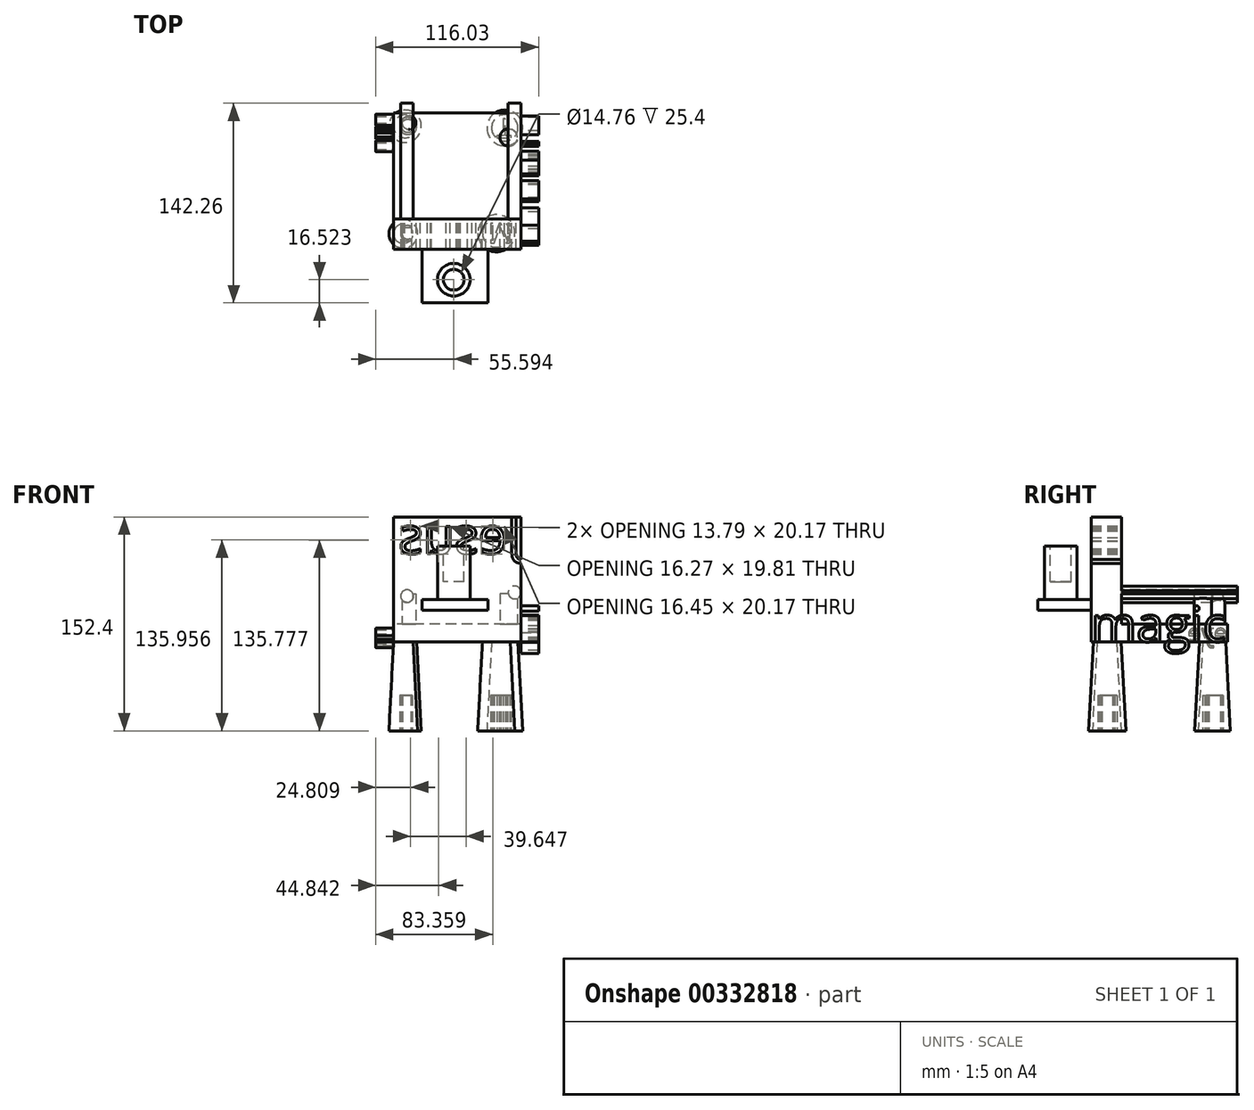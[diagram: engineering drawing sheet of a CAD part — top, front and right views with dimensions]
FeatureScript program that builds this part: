
annotation { "Feature Type Name" : "Feature", "Feature Type Description" : "" }
export const myFeature = defineFeature(function(context is Context, id is Id, definition is map)
    precondition{}
    {
        {
            var Q0;
            Q0=qCreatedBy(makeId("Top.planeOp"),FACE);
            var sketch = newSketch(context, id + "F0", { "sketchPlane" : qUnion([Q0])});
            skLineSegment(sketch, "E0.bottom", {"start": v(-47.1, -35.92) * mm, "end": v(43.53, -35.92) * mm});
            skLineSegment(sketch, "E0.top", {"start": v(-47.1, 61.4) * mm, "end": v(43.53, 61.4) * mm});
            skLineSegment(sketch, "E0.left", {"start": v(-47.1, -35.92) * mm, "end": v(-47.1, 61.4) * mm});
            skLineSegment(sketch, "E0.right", {"start": v(43.53, -35.92) * mm, "end": v(43.53, 61.4) * mm});
            skSolve(sketch);
        }
        {
            var Q0;
            Q0=makeQuery(id+"F0.imprint","IMPRINT",FACE,{"disambiguationData":[TD([[makeQuery(id+"F0.imprint","IMPRINT",EDGE,{"derivedFrom":sQuery(id+"F0.wireOp",EDGE,"E0.bottom")}),1.0]])]});
            extrude(context, id + "F1", {"entities" : qUnion([Q0]), "depth" : 12.7 * mm});
        }
        {
            var Q0;
            Q0=makeQuery(id+"F1.opExtrude","CAP_FACE",FACE,{"disambiguationData":[OSD([sQuery(id+"F0.wireOp",EDGE,"E0.bottom"),sQuery(id+"F0.wireOp",EDGE,"E0.top"),sQuery(id+"F0.wireOp",EDGE,"E0.left"),sQuery(id+"F0.wireOp",EDGE,"E0.right")])],"isStart":true});
            var sketch = newSketch(context, id + "F2", { "sketchPlane" : qUnion([Q0])});
            skCircle(sketch, "E1", {"center": v(-38.88, -51.86) * mm, "radius": 8.22 * mm});
            skSolve(sketch);
        }
        {
            var Q0;
            Q0 = qSketchRegion(id + "F2", true);
            extrude(context, id + "F3", {"entities" : qUnion([Q0]), "operationType" : NewBodyOperationType.ADD, "depth" : 63.5 * mm, "hasDraft" : true, "draftAngle" : 3 * degree});
        }
        {
            var Q0;
            Q0=makeQuery(id+"F1.opExtrude","CAP_FACE",FACE,{"disambiguationData":[OSD([sQuery(id+"F0.wireOp",EDGE,"E0.bottom"),sQuery(id+"F0.wireOp",EDGE,"E0.top"),sQuery(id+"F0.wireOp",EDGE,"E0.left"),sQuery(id+"F0.wireOp",EDGE,"E0.right")])],"isStart":true});
            var sketch = newSketch(context, id + "F4", { "sketchPlane" : qUnion([Q0])});
            skCircle(sketch, "E2", {"center": v(32.14, -50.66) * mm, "radius": 9.41 * mm});
            skSolve(sketch);
        }
        {
            var Q0;
            Q0 = qSketchRegion(id + "F4", true);
            extrude(context, id + "F5", {"entities" : qUnion([Q0]), "operationType" : NewBodyOperationType.ADD, "depth" : 63.5 * mm, "hasDraft" : true, "draftAngle" : 3 * degree});
        }
        {
            var Q0;
            Q0=makeQuery(id+"F1.opExtrude","CAP_FACE",FACE,{"disambiguationData":[OSD([sQuery(id+"F0.wireOp",EDGE,"E0.bottom"),sQuery(id+"F0.wireOp",EDGE,"E0.top"),sQuery(id+"F0.wireOp",EDGE,"E0.left"),sQuery(id+"F0.wireOp",EDGE,"E0.right")])],"isStart":true});
            var sketch = newSketch(context, id + "F6", { "sketchPlane" : qUnion([Q0])});
            skCircle(sketch, "E3", {"center": v(-40.2, 24.75) * mm, "radius": 6.9 * mm});
            skSolve(sketch);
        }
        {
            var Q0;
            Q0 = qSketchRegion(id + "F6", true);
            extrude(context, id + "F7", {"entities" : qUnion([Q0]), "operationType" : NewBodyOperationType.ADD, "depth" : 63.5 * mm, "hasDraft" : true, "draftAngle" : 3 * degree});
        }
        {
            var Q0;
            Q0=makeQuery(id+"F1.opExtrude","CAP_FACE",FACE,{"disambiguationData":[OSD([sQuery(id+"F0.wireOp",EDGE,"E0.bottom"),sQuery(id+"F0.wireOp",EDGE,"E0.top"),sQuery(id+"F0.wireOp",EDGE,"E0.left"),sQuery(id+"F0.wireOp",EDGE,"E0.right")])],"isStart":true});
            var sketch = newSketch(context, id + "F8", { "sketchPlane" : qUnion([Q0])});
            skCircle(sketch, "E4", {"center": v(26.11, 24.38) * mm, "radius": 9.9 * mm});
            skSolve(sketch);
        }
        {
            var Q0;
            Q0 = qSketchRegion(id + "F8", true);
            extrude(context, id + "F9", {"entities" : qUnion([Q0]), "operationType" : NewBodyOperationType.ADD, "depth" : 63.5 * mm, "hasDraft" : true, "draftAngle" : 3 * degree});
        }
        {
            var Q0;
            Q0=makeQuery(id+"F1.opExtrude","CAP_FACE",FACE,{"disambiguationData":[OSD([sQuery(id+"F0.wireOp",EDGE,"E0.bottom"),sQuery(id+"F0.wireOp",EDGE,"E0.top"),sQuery(id+"F0.wireOp",EDGE,"E0.left"),sQuery(id+"F0.wireOp",EDGE,"E0.right")])],"isStart":false});
            var sketch = newSketch(context, id + "F10", { "sketchPlane" : qUnion([Q0])});
            skLineSegment(sketch, "E5.bottom", {"start": v(43.53, -14.31) * mm, "end": v(-47.1, -14.31) * mm});
            skLineSegment(sketch, "E5.top", {"start": v(43.53, -35.92) * mm, "end": v(-47.1, -35.92) * mm});
            skLineSegment(sketch, "E5.left", {"start": v(43.53, -14.31) * mm, "end": v(43.53, -35.92) * mm});
            skLineSegment(sketch, "E5.right", {"start": v(-47.1, -14.31) * mm, "end": v(-47.1, -35.92) * mm});
            skSolve(sketch);
        }
        {
            var Q0;
            Q0 = qSketchRegion(id + "F10", true);
            extrude(context, id + "F11", {"entities" : qUnion([Q0]), "operationType" : NewBodyOperationType.ADD, "depth" : 76.2 * mm});
        }
        {
            var Q0;
            Q0=makeQuery(id+"F11.opExtrude","SWEPT_FACE",FACE,{"disambiguationData":[OSD([sQuery(id+"F10.wireOp",EDGE,"E5.bottom")])]});
            var sketch = newSketch(context, id + "F12", { "sketchPlane" : qUnion([Q0])});
            skCircle(sketch, "E6", {"center": v(-39.12, 35.17) * mm, "radius": 4.54 * mm});
            skSolve(sketch);
        }
        {
            var Q0;
            {var subQ0=sQuery(id+"F12.wireOp",EDGE,"E6");var subQ1=makeQuery(id+"F11.opExtrude","SWEPT_EDGE",EDGE,{"disambiguationData":[OSD([sQuery(id+"F0.wireOp",EDGE,"E0.right"),sQuery(id+"F10.wireOp",EDGE,"E5.bottom"),sQuery(id+"F10.wireOp",EDGE,"E5.left")])]});var subQ2=makeQuery(id+"F12.imprint","INTERSECT",VERTEX,{"disambiguationData":[OD(0.0)],"derivedFrom":[subQ1,subQ0]});Q0=makeQuery(id+"F12.imprint","IMPRINT",FACE,{"disambiguationData":[TD([[makeQuery(id+"F12.imprint","IMPRINT",EDGE,{"disambiguationData":[TD([[subQ2,1.0]])],"derivedFrom":subQ0}),1.0]])]});}
            extrude(context, id + "F13", {"entities" : qUnion([Q0]), "operationType" : NewBodyOperationType.ADD, "depth" : 82.55 * mm});
        }
        {
            var Q0;
            Q0=makeQuery(id+"F11.opExtrude","SWEPT_FACE",FACE,{"disambiguationData":[OSD([sQuery(id+"F10.wireOp",EDGE,"E5.bottom")])]});
            var sketch = newSketch(context, id + "F14", { "sketchPlane" : qUnion([Q0])});
            skCircle(sketch, "E7", {"center": v(37.5, 32.5) * mm, "radius": 4.5 * mm});
            skSolve(sketch);
        }
        {
            var Q0;
            Q0=makeQuery(id+"F14.imprint","IMPRINT",FACE,{"disambiguationData":[TD([[makeQuery(id+"F14.imprint","IMPRINT",EDGE,{"derivedFrom":sQuery(id+"F14.wireOp",EDGE,"E7")}),1.0]])]});
            extrude(context, id + "F15", {"entities" : qUnion([Q0]), "operationType" : NewBodyOperationType.ADD, "depth" : 82.55 * mm});
        }
        {
            var Q0;
            Q0=makeQuery(id+"F11.opExtrude","SWEPT_FACE",FACE,{"disambiguationData":[OSD([sQuery(id+"F10.wireOp",EDGE,"E5.bottom")])]});
            var sketch = newSketch(context, id + "F16", { "sketchPlane" : qUnion([Q0])});
            skText(sketch, "E8", { "text": "Jesus\n", "fontName": "OpenSans-Regular.ttf"});
            const initialGuessF16  = {"E8": [-0.04353, 0.06273, 1, 0, 0.02617]};
            skSetInitialGuess(sketch, initialGuessF16);
            skSolve(sketch);
        }
        {
            var Q0;
            Q0=makeQuery(id+"F16.imprint","IMPRINT",FACE,{"disambiguationData":[TD([[makeQuery(id+"F16.imprint","IMPRINT",EDGE,{"derivedFrom":sQuery(id+"F16.wireOp",EDGE,"E8.sketch_text.stroke-54")}),-1.0]])]});
            var Q1;
            Q1=makeQuery(id+"F16.imprint","IMPRINT",FACE,{"disambiguationData":[TD([[makeQuery(id+"F16.imprint","IMPRINT",EDGE,{"derivedFrom":sQuery(id+"F16.wireOp",EDGE,"E8.sketch_text.stroke-29")}),-1.0]])]});
            var Q2;
            {var subQ8=sQuery(id+"F16.wireOp",EDGE,"E8.sketch_text.stroke-4");Q2=makeQuery(id+"F16.imprint","IMPRINT",FACE,{"disambiguationData":[TD([[makeQuery(id+"F16.imprint","IMPRINT",EDGE,{"derivedFrom":subQ8}),-1.0]])]});}
            var Q3;
            Q3=makeQuery(id+"F16.imprint","IMPRINT",FACE,{"disambiguationData":[TD([[makeQuery(id+"F16.imprint","IMPRINT",EDGE,{"derivedFrom":sQuery(id+"F16.wireOp",EDGE,"E8.sketch_text.stroke-10")}),-1.0]])]});
            var Q4;
            Q4=makeQuery(id+"F16.imprint","IMPRINT",FACE,{"disambiguationData":[TD([[makeQuery(id+"F16.imprint","IMPRINT",EDGE,{"derivedFrom":sQuery(id+"F16.wireOp",EDGE,"E8.sketch_text.stroke-71")}),-1.0]])]});
            extrude(context, id + "F17", {"entities" : qUnion([Q0, Q1, Q2, Q3, Q4]), "operationType" : NewBodyOperationType.REMOVE, "oppositeDirection" : true, "depth" : 28.28 * mm});
        }
        {
            var Q0;
            {var subQ2=sQuery(id+"F10.wireOp",EDGE,"E5.bottom");var subQ4=sQuery(id+"F0.wireOp",EDGE,"E0.left");Q0=makeQuery(id+"F17.boolean.opBoolean","SPLIT",FACE,{"disambiguationData":[TD([makeQuery(id+"F1.opExtrude","SWEPT_FACE",FACE,{"disambiguationData":[OSD([subQ4])]})])],"derivedFrom":makeQuery(id+"F11.opExtrude","SWEPT_FACE",FACE,{"disambiguationData":[OSD([subQ2])]})});}
            var sketch = newSketch(context, id + "F18", { "sketchPlane" : qUnion([Q0])});
            skSolve(sketch);
        }
        {
            var Q0;
            Q0=makeQuery(id+"F5.opExtrude","CAP_FACE",FACE,{"disambiguationData":[OSD([sQuery(id+"F4.wireOp",EDGE,"E2")])],"isStart":false});
            var sketch = newSketch(context, id + "F19", { "sketchPlane" : qUnion([Q0])});
            skText(sketch, "E9", { "text": "T", "fontName": "OpenSans-Regular.ttf"});
            const initialGuessF19  = {"E9": [0.02645, -0.05722, 1, 0, 0.01368]};
            skSetInitialGuess(sketch, initialGuessF19);
            skSolve(sketch);
        }
        {
            var Q0;
            Q0 = qSketchRegion(id + "F19", true);
            extrude(context, id + "F20", {"entities" : qUnion([Q0]), "operationType" : NewBodyOperationType.REMOVE, "oppositeDirection" : true, "depth" : 25.4 * mm});
        }
        {
            var Q0;
            Q0=makeQuery(id+"F3.opExtrude","CAP_FACE",FACE,{"disambiguationData":[OSD([sQuery(id+"F2.wireOp",EDGE,"E1")])],"isStart":false});
            var sketch = newSketch(context, id + "F21", { "sketchPlane" : qUnion([Q0])});
            skText(sketch, "E10", { "text": "C", "fontName": "OpenSans-Regular.ttf"});
            const initialGuessF21  = {"E10": [-0.04366, -0.0579, 1, 0, 0.01173]};
            skSetInitialGuess(sketch, initialGuessF21);
            skSolve(sketch);
        }
        {
            var Q0;
            Q0 = qSketchRegion(id + "F21", true);
            extrude(context, id + "F22", {"entities" : qUnion([Q0]), "operationType" : NewBodyOperationType.REMOVE, "oppositeDirection" : true, "depth" : 25.4 * mm});
        }
        {
            var Q0;
            Q0=makeQuery(id+"F7.opExtrude","CAP_FACE",FACE,{"disambiguationData":[OSD([sQuery(id+"F6.wireOp",EDGE,"E3")])],"isStart":false});
            var sketch = newSketch(context, id + "F23", { "sketchPlane" : qUnion([Q0])});
            skText(sketch, "E11", { "text": "C", "fontName": "OpenSans-Regular.ttf"});
            const initialGuessF23  = {"E11": [-0.043, 0.01915, 1, 0, 0.01066]};
            skSetInitialGuess(sketch, initialGuessF23);
            skSolve(sketch);
        }
        {
            var Q0;
            Q0 = qSketchRegion(id + "F23", true);
            extrude(context, id + "F24", {"entities" : qUnion([Q0]), "operationType" : NewBodyOperationType.REMOVE, "oppositeDirection" : true, "depth" : 25.4 * mm});
        }
        {
            var Q0;
            Q0=makeQuery(id+"F9.opExtrude","CAP_FACE",FACE,{"disambiguationData":[OSD([sQuery(id+"F8.wireOp",EDGE,"E4")])],"isStart":false});
            var sketch = newSketch(context, id + "F25", { "sketchPlane" : qUnion([Q0])});
            skText(sketch, "E12", { "text": "M", "fontName": "OpenSans-Regular.ttf"});
            const initialGuessF25  = {"E12": [0.02017, 0.01745, 1, 0, 0.01387]};
            skSetInitialGuess(sketch, initialGuessF25);
            skSolve(sketch);
        }
        {
            var Q0;
            Q0 = qSketchRegion(id + "F25", true);
            extrude(context, id + "F26", {"entities" : qUnion([Q0]), "operationType" : NewBodyOperationType.REMOVE, "oppositeDirection" : true, "depth" : 25.4 * mm});
        }
        {
            var Q0;
            {var subQ0=sQuery(id+"F0.wireOp",EDGE,"E0.top");var subQ1=sQuery(id+"F10.wireOp",EDGE,"E5.bottom");var subQ2=sQuery(id+"F0.wireOp",EDGE,"E0.right");var subQ6=sQuery(id+"F10.wireOp",EDGE,"E5.left");Q0=makeQuery(id+"F17.boolean.opBoolean","SPLIT",FACE,{"disambiguationData":[TD([makeQuery(id+"F1.opExtrude","SWEPT_FACE",FACE,{"disambiguationData":[OSD([subQ0])]})])],"derivedFrom":makeQuery(id+"F13.boolean.opBoolean","MERGE",FACE,{"derivedFrom":[makeQuery(id+"F11.boolean.opBoolean","MERGE",FACE,{"derivedFrom":[makeQuery(id+"F1.opExtrude","SWEPT_FACE",FACE,{"disambiguationData":[OSD([subQ2])]}),makeQuery(id+"F11.opExtrude","SWEPT_FACE",FACE,{"disambiguationData":[OSD([subQ6])]})]}),makeQuery(id+"F13.opExtrude","SWEPT_FACE",FACE,{"disambiguationData":[OSD([subQ2,subQ1,subQ6])]})]})});}
            var sketch = newSketch(context, id + "F27", { "sketchPlane" : qUnion([Q0])});
            skText(sketch, "E13", { "text": "magic", "fontName": "OpenSans-Regular.ttf"});
            const initialGuessF27  = {"E13": [-0.03592, 0, 1, 0, 0.02508]};
            skSetInitialGuess(sketch, initialGuessF27);
            skSolve(sketch);
        }
        {
            var Q0;
            Q0 = qSketchRegion(id + "F27", true);
            extrude(context, id + "F28", {"entities" : qUnion([Q0]), "operationType" : NewBodyOperationType.ADD, "depth" : 12.7 * mm});
        }
        {
            var Q0;
            Q0=makeQuery(id+"F11.boolean.opBoolean","MERGE",FACE,{"derivedFrom":[makeQuery(id+"F1.opExtrude","SWEPT_FACE",FACE,{"disambiguationData":[OSD([sQuery(id+"F0.wireOp",EDGE,"E0.left")])]}),makeQuery(id+"F11.opExtrude","SWEPT_FACE",FACE,{"disambiguationData":[OSD([sQuery(id+"F10.wireOp",EDGE,"E5.right")])]})]});
            var sketch = newSketch(context, id + "F29", { "sketchPlane" : qUnion([Q0])});
            skText(sketch, "E14", { "text": "eye\n", "fontName": "OpenSans-Regular.ttf"});
            const initialGuessF29  = {"E14": [-0.0614, 0, 1, 0, 0.0127]};
            skSetInitialGuess(sketch, initialGuessF29);
            skSolve(sketch);
        }
        {
            var Q0;
            Q0 = qSketchRegion(id + "F29", true);
            extrude(context, id + "F30", {"entities" : qUnion([Q0]), "operationType" : NewBodyOperationType.ADD, "depth" : 12.7 * mm});
        }
        {
            var Q0;
            Q0=makeQuery(id+"F1.opExtrude","CAP_FACE",FACE,{"disambiguationData":[OSD([sQuery(id+"F0.wireOp",EDGE,"E0.bottom"),sQuery(id+"F0.wireOp",EDGE,"E0.top"),sQuery(id+"F0.wireOp",EDGE,"E0.left"),sQuery(id+"F0.wireOp",EDGE,"E0.right")])],"isStart":false});
            var sketch = newSketch(context, id + "F31", { "sketchPlane" : qUnion([Q0])});
            skCircle(sketch, "E15", {"center": v(-36.14, 54.44) * mm, "radius": 4.98 * mm});
            skSolve(sketch);
        }
        {
            var Q0;
            Q0 = qSketchRegion(id + "F31", true);
            extrude(context, id + "F32", {"entities" : qUnion([Q0]), "operationType" : NewBodyOperationType.ADD, "depth" : 21.59 * mm});
        }
        {
            var Q0;
            Q0=makeQuery(id+"F1.opExtrude","CAP_FACE",FACE,{"disambiguationData":[OSD([sQuery(id+"F0.wireOp",EDGE,"E0.bottom"),sQuery(id+"F0.wireOp",EDGE,"E0.top"),sQuery(id+"F0.wireOp",EDGE,"E0.left"),sQuery(id+"F0.wireOp",EDGE,"E0.right")])],"isStart":false});
            var sketch = newSketch(context, id + "F33", { "sketchPlane" : qUnion([Q0])});
            skCircle(sketch, "E16", {"center": v(34.91, 43.84) * mm, "radius": 6.2 * mm});
            skSolve(sketch);
        }
        {
            var Q0;
            Q0 = qSketchRegion(id + "F33", true);
            extrude(context, id + "F34", {"entities" : qUnion([Q0]), "operationType" : NewBodyOperationType.ADD, "depth" : 21.59 * mm});
        }
        {
            var Q0;
            {var subQ0=sQuery(id+"F0.wireOp",EDGE,"E0.left");var subQ5=sQuery(id+"F0.wireOp",EDGE,"E0.bottom");var subQ6=sQuery(id+"F10.wireOp",EDGE,"E5.top");Q0=makeQuery(id+"F17.boolean.opBoolean","SPLIT",FACE,{"disambiguationData":[TD([makeQuery(id+"F1.opExtrude","SWEPT_FACE",FACE,{"disambiguationData":[OSD([subQ0])]})])],"derivedFrom":makeQuery(id+"F11.boolean.opBoolean","MERGE",FACE,{"derivedFrom":[makeQuery(id+"F1.opExtrude","SWEPT_FACE",FACE,{"disambiguationData":[OSD([subQ5])]}),makeQuery(id+"F11.opExtrude","SWEPT_FACE",FACE,{"disambiguationData":[OSD([subQ6])]})]})});}
            var sketch = newSketch(context, id + "F35", { "sketchPlane" : qUnion([Q0])});
            skLineSegment(sketch, "E17.bottom", {"start": v(-26.87, 22.3) * mm, "end": v(20.1, 22.3) * mm});
            skLineSegment(sketch, "E17.top", {"start": v(-26.87, 29.97) * mm, "end": v(20.1, 29.97) * mm});
            skLineSegment(sketch, "E17.left", {"start": v(-26.87, 22.3) * mm, "end": v(-26.87, 29.97) * mm});
            skLineSegment(sketch, "E17.right", {"start": v(20.1, 22.3) * mm, "end": v(20.1, 29.97) * mm});
            skSolve(sketch);
        }
        {
            var Q0;
            Q0 = qSketchRegion(id + "F35", true);
            extrude(context, id + "F36", {"entities" : qUnion([Q0]), "operationType" : NewBodyOperationType.ADD, "depth" : 38.1 * mm});
        }
        {
            var Q0;
            Q0=makeQuery(id+"F36.opExtrude","SWEPT_FACE",FACE,{"disambiguationData":[OSD([sQuery(id+"F35.wireOp",EDGE,"E17.top")])]});
            var sketch = newSketch(context, id + "F37", { "sketchPlane" : qUnion([Q0])});
            skCircle(sketch, "E18", {"center": v(-4.2, -57.5) * mm, "radius": 11.62 * mm});
            skSolve(sketch);
        }
        {
            var Q0;
            Q0 = qSketchRegion(id + "F37", true);
            extrude(context, id + "F38", {"entities" : qUnion([Q0]), "operationType" : NewBodyOperationType.ADD, "depth" : 38.1 * mm});
        }
        {
            var Q0;
            Q0=makeQuery(id+"F38.opExtrude","CAP_FACE",FACE,{"disambiguationData":[OSD([sQuery(id+"F37.wireOp",EDGE,"E18")])],"isStart":false});
            var sketch = newSketch(context, id + "F39", { "sketchPlane" : qUnion([Q0])});
            skCircle(sketch, "E19", {"center": v(-4.2, -57.5) * mm, "radius": 7.38 * mm});
            skSolve(sketch);
        }
        {
            var Q0;
            Q0 = qSketchRegion(id + "F39", true);
            extrude(context, id + "F40", {"entities" : qUnion([Q0]), "operationType" : NewBodyOperationType.REMOVE, "oppositeDirection" : true, "depth" : 25.4 * mm});
        }
    });
